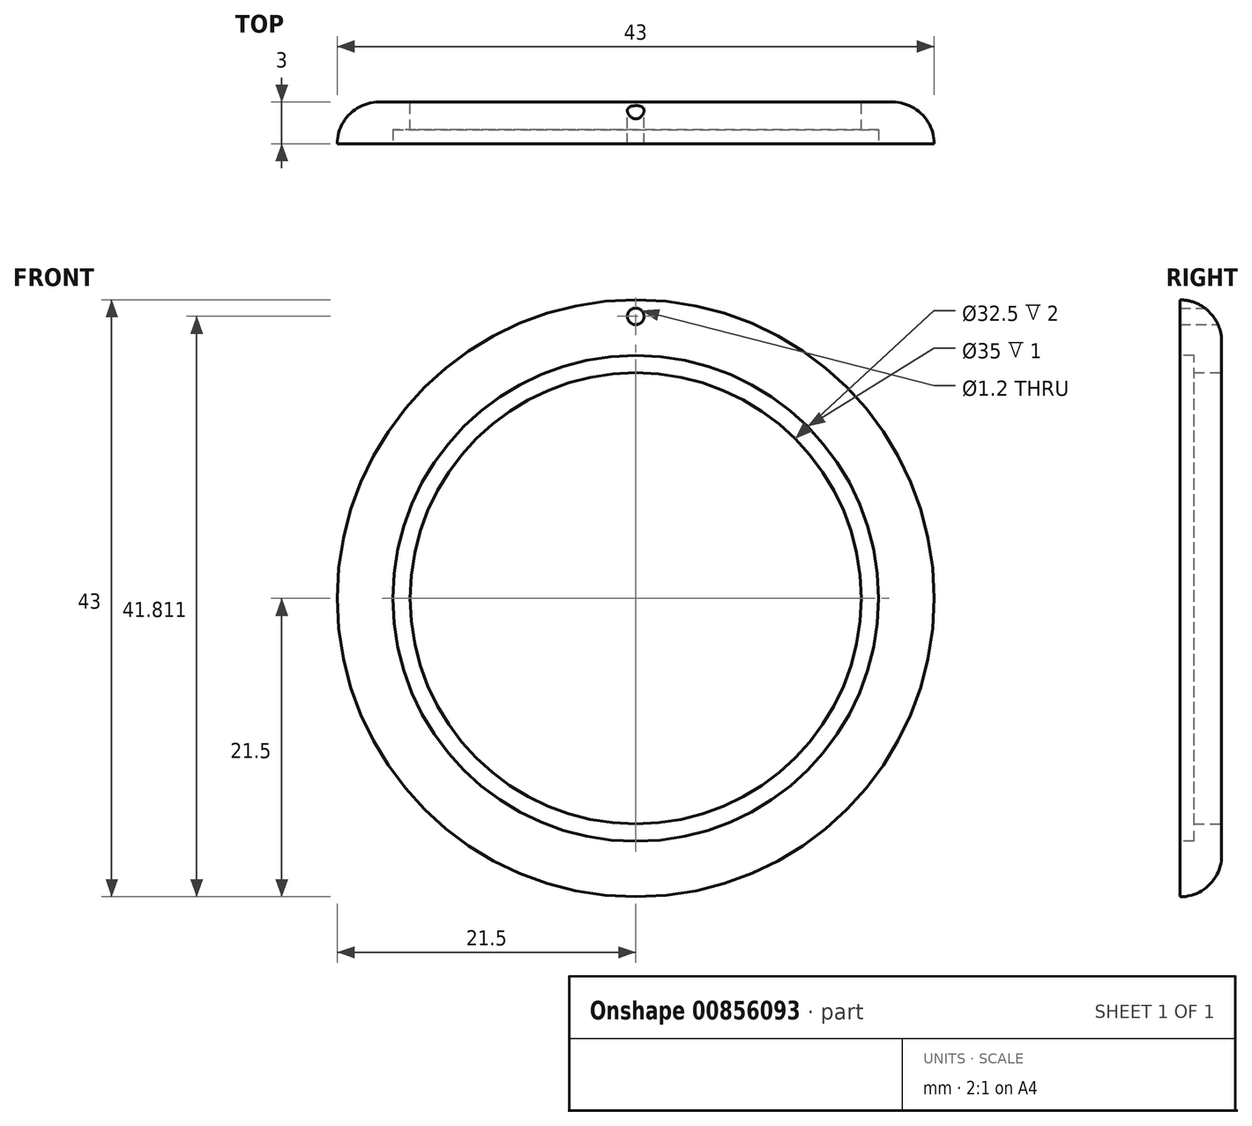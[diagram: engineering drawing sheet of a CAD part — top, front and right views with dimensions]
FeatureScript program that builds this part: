
annotation { "Feature Type Name" : "Feature", "Feature Type Description" : "" }
export const myFeature = defineFeature(function(context is Context, id is Id, definition is map)
    precondition{}
    {
        {
            var Q0;
            Q0=qCreatedBy(makeId("Front.planeOp"),FACE);
            var sketch = newSketch(context, id + "F0", { "sketchPlane" : qUnion([Q0])});
            skCircle(sketch, "E0", {"center": v(0, 0) * mm, "radius": 21.5 * mm});
            skSolve(sketch);
        }
        {
            var Q0;
            Q0=makeQuery(id+"F0.imprint","IMPRINT",FACE,{"disambiguationData":[TD([[makeQuery(id+"F0.imprint","IMPRINT",EDGE,{"derivedFrom":sQuery(id+"F0.wireOp",EDGE,"E0")}),1.0]])]});
            extrude(context, id + "F1", {"entities" : qUnion([Q0]), "oppositeDirection" : true, "depth" : 3 * mm, "offsetDistance" : 25 * mm});
        }
        {
            var Q0;
            Q0=makeQuery(id+"F1.opExtrude","CAP_FACE",FACE,{"disambiguationData":[OSD([sQuery(id+"F0.wireOp",EDGE,"E0")])],"isStart":false});
            var sketch = newSketch(context, id + "F2", { "sketchPlane" : qUnion([Q0])});
            skCircle(sketch, "E1", {"center": v(0, 0) * mm, "radius": 16.25 * mm});
            skSolve(sketch);
        }
        {
            var Q0;
            Q0=sQuery(id+"F2.wireOp",VERTEX,"E1.center");
            var Q1;
            Q1=makeQuery(id+"F1.opExtrude","SWEPT_BODY",BODY,{"disambiguationData":[OSD([sQuery(id+"F0.wireOp",EDGE,"E0")])]});
            hole(context, id + "F3", {"style" : HoleStyle.SIMPLE, "endStyle" : HoleEndStyle.THROUGH, "holeDiameter" : 32.5 * mm, "majorDiameter" : 5 * mm, "isTappedThrough" : true, "tappedDepth" : 12 * mm, "tapClearance" : 3, "startFromSketch" : true, "locations" : qUnion([Q0]), "scope" : qUnion([Q1])});
        }
        {
            var Q0;
            Q0=makeQuery(id+"F1.opExtrude","CAP_EDGE",EDGE,{"disambiguationData":[OSD([sQuery(id+"F0.wireOp",EDGE,"E0")])],"isStart":false});
            fillet(context, id + "F4", {"entities" : qUnion([Q0]), "radius" : 3 * mm, "tangentPropagation" : true, "allowEdgeOverflow" : false});
        }
        {
            var Q0;
            Q0=qCreatedBy(makeId("Front.planeOp"),FACE);
            var sketch = newSketch(context, id + "F5", { "sketchPlane" : qUnion([Q0])});
            skCircle(sketch, "E2", {"center": v(0, 0) * mm, "radius": 17.5 * mm});
            skSolve(sketch);
        }
        {
            var Q0;
            Q0=makeQuery(id+"F1.opExtrude","CAP_FACE",FACE,{"disambiguationData":[OSD([sQuery(id+"F0.wireOp",EDGE,"E0")])],"isStart":false});
            var sketch = newSketch(context, id + "F6", { "sketchPlane" : qUnion([Q0])});
            skPoint(sketch, "E3", {"position": v(0, 20.31) * mm});
            skSolve(sketch);
        }
        {
            var Q0;
            Q0=makeQuery(id+"F5.imprint","IMPRINT",FACE,{"disambiguationData":[TD([[makeQuery(id+"F5.imprint","IMPRINT",EDGE,{"derivedFrom":sQuery(id+"F5.wireOp",EDGE,"E2")}),1.0]])]});
            var Q1;
            Q1=sQuery(id+"F5.wireOp",EDGE,"E2");
            extrude(context, id + "F7", {"entities" : qUnion([Q0]), "operationType" : NewBodyOperationType.REMOVE, "surfaceEntities" : qUnion([Q1]), "oppositeDirection" : true, "depth" : 1 * mm, "offsetDistance" : 25 * mm});
        }
        {
            var Q0;
            Q0=sQuery(id+"F6.wireOp",VERTEX,"E3");
            var Q1;
            Q1=makeQuery(id+"F1.opExtrude","SWEPT_BODY",BODY,{"disambiguationData":[OSD([sQuery(id+"F0.wireOp",EDGE,"E0")])]});
            hole(context, id + "F8", {"style" : HoleStyle.C_BORE, "endStyle" : HoleEndStyle.BLIND, "holeDiameter" : 1.2 * mm, "cBoreDiameter" : 1.2 * mm, "cBoreDepth" : .8 * mm, "majorDiameter" : 5 * mm, "holeDepth" : 3.5 * mm, "isTappedThrough" : true, "tappedDepth" : 12 * mm, "tapClearance" : 3, "startFromSketch" : true, "locations" : qUnion([Q0]), "scope" : qUnion([Q1])});
        }
    });
